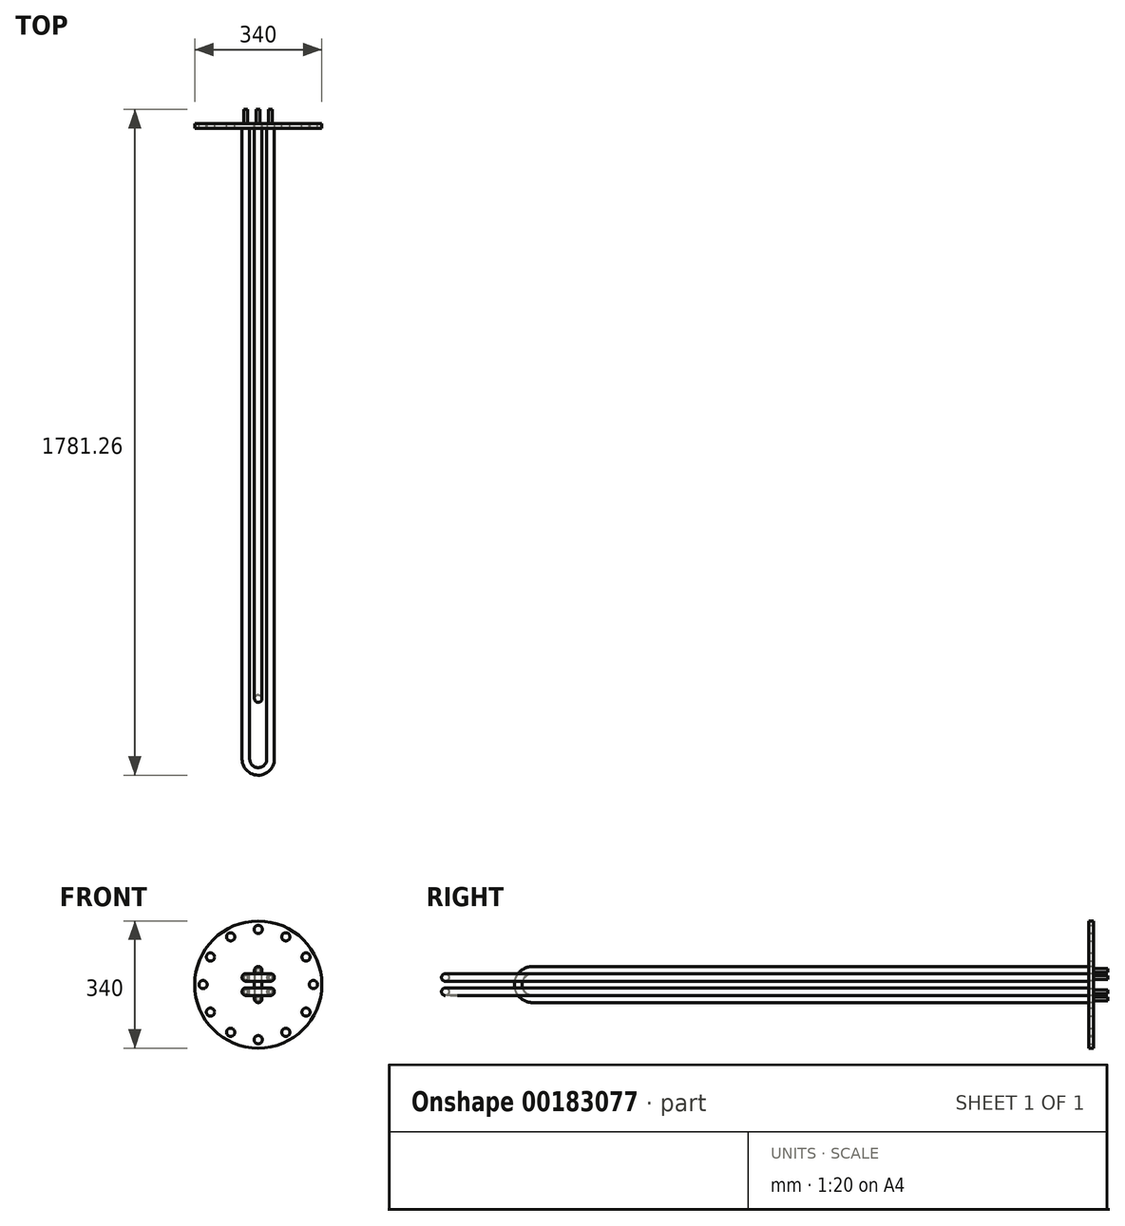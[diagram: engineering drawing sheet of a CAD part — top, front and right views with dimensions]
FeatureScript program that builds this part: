
annotation { "Feature Type Name" : "Feature", "Feature Type Description" : "" }
export const myFeature = defineFeature(function(context is Context, id is Id, definition is map)
    precondition{}
    {
        {
            var Q0;
            Q0=qCreatedBy(makeId("Front.planeOp"),FACE);
            var sketch = newSketch(context, id + "F0", { "sketchPlane" : qUnion([Q0])});
            skCircle(sketch, "E0", {"center": v(0, 0) * mm, "radius": 170 * mm});
            skCircle(sketch, "E1", {"center": v(0, 38.1) * mm, "radius": 10.16 * mm});
            skCircle(sketch, "E2.1.0", {"center": v(-33, 19.05) * mm, "radius": 10.16 * mm});
            skCircle(sketch, "E2.2.0", {"center": v(-33, -19.05) * mm, "radius": 10.16 * mm});
            skCircle(sketch, "E2.3.0", {"center": v(0, -38.1) * mm, "radius": 10.16 * mm});
            skCircle(sketch, "E2.4.0", {"center": v(33, -19.05) * mm, "radius": 10.16 * mm});
            skCircle(sketch, "E2.5.0", {"center": v(33, 19.05) * mm, "radius": 10.16 * mm});
            skSolve(sketch);
        }
        {
            var Q0;
            Q0 = qSketchRegion(id + "F0", true);
            extrude(context, id + "F1", {"entities" : qUnion([Q0]), "depth" : 12.7 * mm});
        }
        {
            var Q0;
            Q0=qCreatedBy(makeId("Right.planeOp"),FACE);
            var sketch = newSketch(context, id + "F2", { "sketchPlane" : qUnion([Q0])});
            skLineSegment(sketch, "E3", {"start": v(0, 38.1) * mm, "end": v(-1500, 38.1) * mm});
            skLineSegment(sketch, "E4", {"start": v(0, -38.1) * mm, "end": v(-1500, -38.1) * mm});
            skArc(sketch, "E5", {"start": v(-1500, 38.1) * mm, "mid": v(-1538.1, 0) * mm, "end": v(-1500, -38.1) * mm});
            skSolve(sketch);
        }
        {
            var Q0;
            Q0=qCreatedBy(makeId("Front.planeOp"),FACE);
            var sketch = newSketch(context, id + "F3", { "sketchPlane" : qUnion([Q0])});
            skCircle(sketch, "E6.0", {"center": v(0, 38.1) * mm, "radius": 10.16 * mm});
            skCircle(sketch, "E7", {"center": v(0, 38.1) * mm, "radius": 9.53 * mm});
            skSolve(sketch);
        }
        {
            var Q0;
            Q0 = qSketchRegion(id + "F3", true);
            var Q1;
            Q1 = qConstructionFilter(qBodyType(qCreatedBy(id + "F2" ,EDGE), BodyType.WIRE), ConstructionObject.NO);
            sweep(context, id + "F4", {"operationType" : NewBodyOperationType.ADD, "profiles" : qUnion([Q0]), "path" : qUnion([Q1])});
        }
        {
            var Q0;
            Q0=qCreatedBy(makeId("Top.planeOp"),FACE);
            cPlane(context, id + "F5", {"entities" : qUnion([Q0]), "cplaneType" : CPlaneType.OFFSET, "offset" : 19.05 * mm, "width" : 152.4 * mm, "height" : 152.4 * mm});
        }
        {
            var Q0;
            Q0=qCreatedBy(id+"F5.planeOp",FACE);
            var sketch = newSketch(context, id + "F6", { "sketchPlane" : qUnion([Q0])});
            skLineSegment(sketch, "E8", {"start": v(-33, 0) * mm, "end": v(-33, -1700) * mm});
            skLineSegment(sketch, "E9", {"start": v(33, 0) * mm, "end": v(33, -1700) * mm});
            skArc(sketch, "E10", {"start": v(-33, -1700) * mm, "mid": v(0, -1733) * mm, "end": v(33, -1700) * mm});
            skSolve(sketch);
        }
        {
            var Q0;
            Q0=qCreatedBy(makeId("Front.planeOp"),FACE);
            var sketch = newSketch(context, id + "F7", { "sketchPlane" : qUnion([Q0])});
            skCircle(sketch, "E11.0", {"center": v(33, 19.05) * mm, "radius": 10.16 * mm});
            skCircle(sketch, "E12", {"center": v(33, 19.05) * mm, "radius": 9.53 * mm});
            skSolve(sketch);
        }
        {
            var Q0;
            Q0 = qSketchRegion(id + "F7", true);
            var Q1;
            Q1 = qConstructionFilter(qBodyType(qCreatedBy(id + "F6" ,EDGE), BodyType.WIRE), ConstructionObject.NO);
            sweep(context, id + "F8", {"operationType" : NewBodyOperationType.ADD, "profiles" : qUnion([Q0]), "path" : qUnion([Q1])});
        }
        {
            var Q0;
            Q0=qCreatedBy(makeId("Top.planeOp"),FACE);
            cPlane(context, id + "F9", {"entities" : qUnion([Q0]), "cplaneType" : CPlaneType.OFFSET, "offset" : 19.05 * mm, "oppositeDirection" : true, "width" : 152.4 * mm, "height" : 152.4 * mm});
        }
        {
            var Q0;
            Q0=qCreatedBy(id+"F9.planeOp",FACE);
            var sketch = newSketch(context, id + "F10", { "sketchPlane" : qUnion([Q0])});
            skLineSegment(sketch, "E13", {"start": v(-33, 0) * mm, "end": v(-33, -1700) * mm});
            skLineSegment(sketch, "E14", {"start": v(33, 0) * mm, "end": v(33, -1700) * mm});
            skArc(sketch, "E15", {"start": v(-33, -1700) * mm, "mid": v(0, -1733) * mm, "end": v(33, -1700) * mm});
            skSolve(sketch);
        }
        {
            var Q0;
            Q0=qCreatedBy(makeId("Front.planeOp"),FACE);
            var sketch = newSketch(context, id + "F11", { "sketchPlane" : qUnion([Q0])});
            skCircle(sketch, "E16.0", {"center": v(33, -19.05) * mm, "radius": 10.16 * mm});
            skCircle(sketch, "E17", {"center": v(33, -19.05) * mm, "radius": 9.53 * mm});
            skSolve(sketch);
        }
        {
            var Q0;
            Q0 = qSketchRegion(id + "F11", true);
            var Q1;
            Q1 = qConstructionFilter(qBodyType(qCreatedBy(id + "F10" ,EDGE), BodyType.WIRE), ConstructionObject.NO);
            sweep(context, id + "F12", {"operationType" : NewBodyOperationType.ADD, "profiles" : qUnion([Q0]), "path" : qUnion([Q1])});
        }
        {
            var Q0;
            Q0=qCreatedBy(makeId("Front.planeOp"),FACE);
            var sketch = newSketch(context, id + "F13", { "sketchPlane" : qUnion([Q0])});
            skCircle(sketch, "E18", {"center": v(0, 38.1) * mm, "radius": 5.08 * mm});
            skSolve(sketch);
        }
        {
            var Q0;
            Q0 = qSketchRegion(id + "F13", true);
            extrude(context, id + "F14", {"entities" : qUnion([Q0]), "oppositeDirection" : true, "depth" : 38.1 * mm});
        }
        {
            var Q0;
            Q0=qCreatedBy(makeId("Right.planeOp"),FACE);
            var sketch = newSketch(context, id + "F15", { "sketchPlane" : qUnion([Q0])});
            skLineSegment(sketch, "E19", {"start": v(75.85, 0) * mm, "end": v(0, 0) * mm});
            skSolve(sketch);
        }
        {
            var Q0;
            Q0=makeQuery(id+"F14.opExtrude","SWEPT_BODY",BODY,{"disambiguationData":[OSD([sQuery(id+"F13.wireOp",EDGE,"E18")])]});
            var Q1;
            Q1=sQuery(id+"F15.wireOp",EDGE,"E19");
            circularPattern(context, id + "F16", {"entities" : qUnion([Q0]), "axis" : qUnion([Q1]), "angle" : 360 * degree, "instanceCount" : 6, "equalSpace" : true});
        }
        {
            var Q0;
            Q0=makeQuery(id+"F0.imprint","IMPRINT",FACE,{"disambiguationData":[TD([[makeQuery(id+"F0.imprint","IMPRINT",EDGE,{"derivedFrom":sQuery(id+"F0.wireOp",EDGE,"E0")}),1.0]])]});
            var sketch = newSketch(context, id + "F17", { "sketchPlane" : qUnion([Q0])});
            skCircle(sketch, "E20", {"center": v(0, 147.5) * mm, "radius": 11 * mm});
            skCircle(sketch, "E21.1.0", {"center": v(-73.75, 127.74) * mm, "radius": 11 * mm});
            skCircle(sketch, "E21.2.0", {"center": v(-127.74, 73.75) * mm, "radius": 11 * mm});
            skCircle(sketch, "E21.3.0", {"center": v(-147.5, 0) * mm, "radius": 11 * mm});
            skCircle(sketch, "E21.4.0", {"center": v(-127.74, -73.75) * mm, "radius": 11 * mm});
            skCircle(sketch, "E21.5.0", {"center": v(-73.75, -127.74) * mm, "radius": 11 * mm});
            skCircle(sketch, "E21.6.0", {"center": v(0, -147.5) * mm, "radius": 11 * mm});
            skCircle(sketch, "E21.7.0", {"center": v(73.75, -127.74) * mm, "radius": 11 * mm});
            skCircle(sketch, "E21.8.0", {"center": v(127.74, -73.75) * mm, "radius": 11 * mm});
            skCircle(sketch, "E21.9.0", {"center": v(147.5, 0) * mm, "radius": 11 * mm});
            skCircle(sketch, "E21.10.0", {"center": v(127.74, 73.75) * mm, "radius": 11 * mm});
            skCircle(sketch, "E21.11.0", {"center": v(73.75, 127.74) * mm, "radius": 11 * mm});
            skPoint(sketch, "E21.center", {"position": v(0, 0) * mm});
            skSolve(sketch);
        }
        {
            var Q0;
            Q0 = qSketchRegion(id + "F17", true);
            extrude(context, id + "F18", {"entities" : qUnion([Q0]), "operationType" : NewBodyOperationType.REMOVE, "depth" : 25 * mm});
        }
    });
